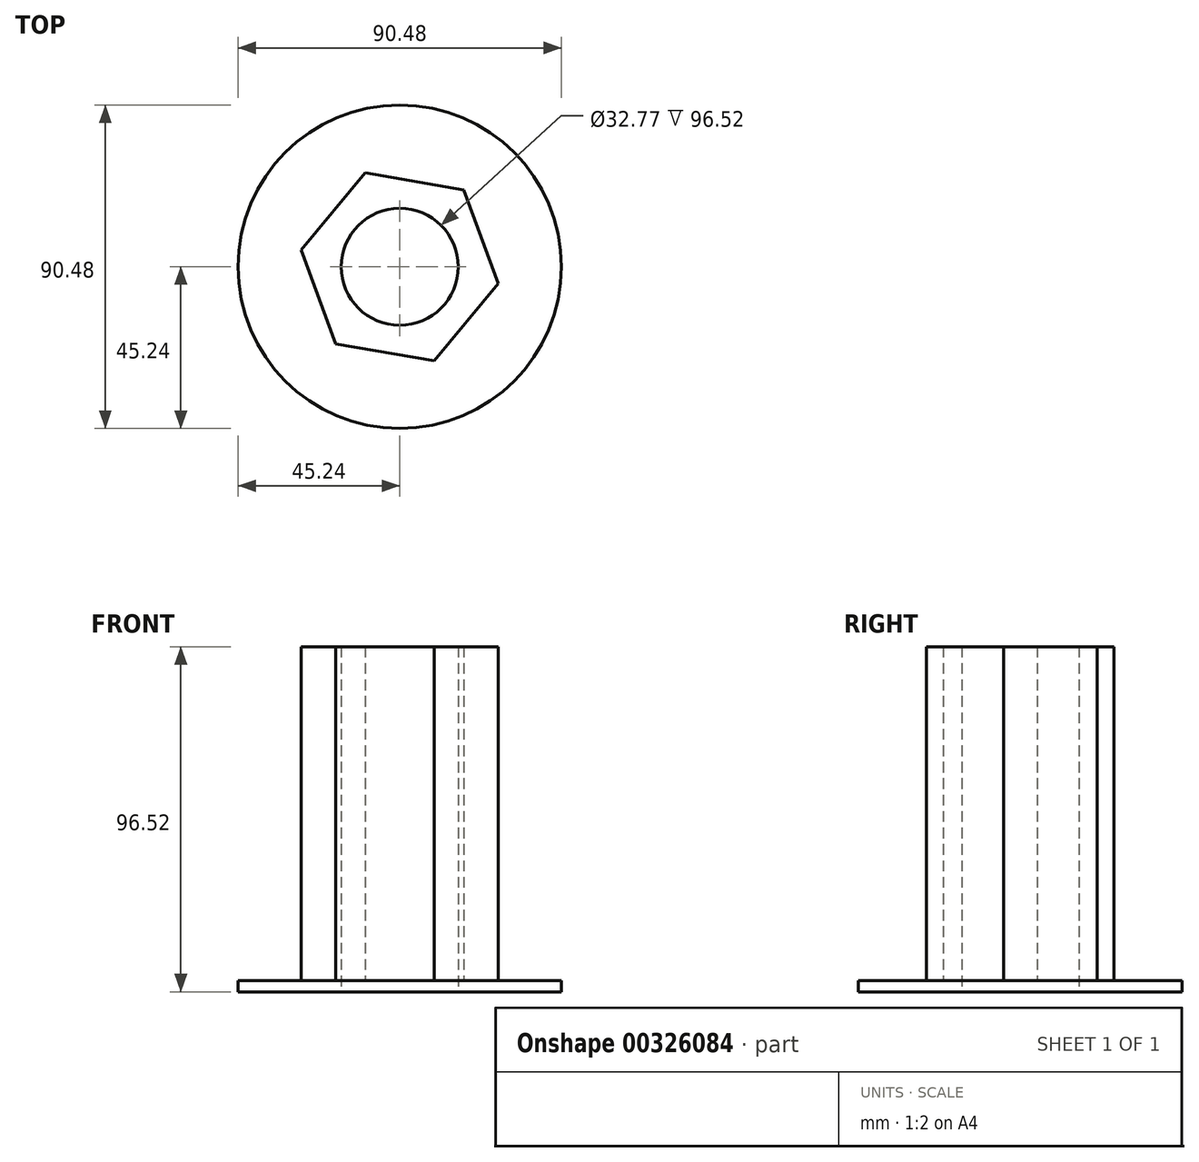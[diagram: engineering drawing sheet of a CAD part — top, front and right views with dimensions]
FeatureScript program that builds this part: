
annotation { "Feature Type Name" : "Feature", "Feature Type Description" : "" }
export const myFeature = defineFeature(function(context is Context, id is Id, definition is map)
    precondition{}
    {
        {
            var Q0;
            Q0=qCreatedBy(makeId("Top.planeOp"),FACE);
            var sketch = newSketch(context, id + "F0", { "sketchPlane" : qUnion([Q0])});
            skCircle(sketch, "E0.cCircle", {"center": v(0, 0) * mm, "radius": 27.98 * mm, "construction": true});
            skLineSegment(sketch, "E0.0", {"start": v(17.88, 21.52) * mm, "end": v(27.58, -4.72) * mm});
            skLineSegment(sketch, "E0.1", {"start": v(27.58, -4.72) * mm, "end": v(9.7, -26.25) * mm});
            skLineSegment(sketch, "E0.2", {"start": v(9.7, -26.25) * mm, "end": v(-17.88, -21.52) * mm});
            skLineSegment(sketch, "E0.3", {"start": v(-17.88, -21.52) * mm, "end": v(-27.58, 4.72) * mm});
            skLineSegment(sketch, "E0.4", {"start": v(-27.58, 4.72) * mm, "end": v(-9.7, 26.25) * mm});
            skLineSegment(sketch, "E0.5", {"start": v(-9.7, 26.25) * mm, "end": v(17.88, 21.52) * mm});
            skCircle(sketch, "E1", {"center": v(0, 0) * mm, "radius": 45.24 * mm});
            skSolve(sketch);
        }
        {
            var Q0;
            Q0=makeQuery(id+"F0.imprint","IMPRINT",FACE,{"disambiguationData":[TD([[makeQuery(id+"F0.imprint","IMPRINT",EDGE,{"derivedFrom":sQuery(id+"F0.wireOp",EDGE,"E0.0")}),-1.0]])]});
            extrude(context, id + "F1", {"entities" : qUnion([Q0]), "depth" : 96.52 * mm});
        }
        {
            var Q0;
            Q0 = qSketchRegion(id + "F0", true);
            extrude(context, id + "F2", {"entities" : qUnion([Q0]), "operationType" : NewBodyOperationType.ADD, "depth" : 3.17 * mm});
        }
        {
            var Q0;
            Q0=qCreatedBy(makeId("Top.planeOp"),FACE);
            var sketch = newSketch(context, id + "F3", { "sketchPlane" : qUnion([Q0])});
            skPoint(sketch, "E2", {"position": v(0, 0) * mm});
            skSolve(sketch);
        }
        {
            var Q0;
            Q0=sQuery(id+"F3.wireOp",VERTEX,"E2");
            var Q1;
            Q1=makeQuery(id+"F1.opExtrude","SWEPT_BODY",BODY,{"disambiguationData":[OSD([sQuery(id+"F0.wireOp",EDGE,"E0.0"),sQuery(id+"F0.wireOp",EDGE,"E0.1"),sQuery(id+"F0.wireOp",EDGE,"E0.2"),sQuery(id+"F0.wireOp",EDGE,"E0.3"),sQuery(id+"F0.wireOp",EDGE,"E0.4"),sQuery(id+"F0.wireOp",EDGE,"E0.5")])]});
            hole(context, id + "F4", {"style" : HoleStyle.SIMPLE, "endStyle" : HoleEndStyle.THROUGH, "oppositeDirection" : true, "holeDiameter" : 32.77 * mm, "tappedDepth" : 12.7 * mm, "tapClearance" : 3, "locations" : qUnion([Q0]), "scope" : qUnion([Q1])});
        }
    });
